# Revit family: 306_ac6e8514f21645dca7f72db6e31d8c
name_source: partatom
category: Pipe Accessories
units: mm (PartAtom-declared; Revit-internal decimal feet)

## family parameters
Always vertical = Yes
Cut with Voids When Loaded = No
Part Type = Valve - Breaks Into
Round Connector Dimension = Use Diameter
Shared = No
Work Plane-Based = No

## types (8) — shared parameters
CAT0 = Yes
CenSd_DN_6 = 6 mm  [stored 0.019685 ft]
DN = 7 mm  [stored 0.0229659 ft]
Description = 3-way rotary mixing valve 3F, PN6 flange
L2D = 265 mm
L2D_Min = 3048 mm
MC = No
Manufacturer = ESBE
QmdConnectorList = 301;D;302;D
R3 = 2 mm  [stored 0.00656168 ft]
URL = http://www.esbe.eu
W2D = 100 mm
X = 3 mm  [stored 0.00984252 ft]
X2 = 5 mm  [stored 0.0164042 ft]
X__ve = -3 mm  [stored -0.00984252 ft]
Y3 = 4 mm  [stored 0.0131234 ft]
magiPartTypeId = 306
magiProductFamilyId = ac6e8514f21645dca7f72db6e31d8c

## per-type parameters (varying)
| type | C | D | D2 | D3 | DN1 | FD2 | H | H1 | LT2 | MH | MH__ve | R1 | R2 | R4 | W1 | X1 | X1__ve | X3 | X5 | Y2 | Y2__ve | Y4 | Z1 | magiProductId |
| 3F 100-225 | 73 mm | 100 mm | 114 mm | 20 mm  [stored 0.0656168 ft] | 16 mm | 105 mm | 132 mm | 106 mm | 133 mm | 90 mm | -90 mm | 60 mm | 57 mm | 75 mm | 16 mm | 18 mm | -18 mm | 213 mm | 80 mm | 38 mm | -38 mm  [stored -0.124672 ft] | 40 mm | 75 mm | 35e6cae2c78145ac8d085347603f0b |
| 3F 125-280 | 80 mm | 125 mm | 138 mm | 23 mm | 18 mm | 120 mm | 150 mm | 121 mm | 150 mm | 108 mm | -108 mm | 72 mm | 69 mm | 90 mm | 11 mm | 21 mm | -21 mm | 243 mm | 91 mm | 38 mm | -38 mm  [stored -0.124672 ft] | 46 mm | 90 mm | 63c3782494ab404eb88c3043804936 |
| 3F 150-400 | 88 mm | 150 mm | 158 mm | 27 mm | 21 mm | 133 mm | 175 mm | 143 mm | 175 mm | 123 mm | -123 mm | 82 mm | 79 mm | 103 mm | 9 mm  [stored 0.0295276 ft] | 24 mm | -24 mm | 286 mm | 107 mm | 37 mm | -37 mm | 54 mm | 103 mm | c360b451805a4af68f699a7088005f |
| 3F 32-28 | 40 mm | 32 mm | 52 mm | 11 mm | 8 mm  [stored 0.0262467 ft] | 60 mm | 80 mm | 57 mm | 80 mm | 44 mm | -44 mm | 29 mm | 26 mm | 37 mm | 14 mm  [stored 0.0459318 ft] | 15 mm  [stored 0.0492126 ft] | -15 mm | 113 mm | 42 mm | 37 mm | -37 mm | 21 mm | 37 mm | fa7e2451a67c46cd9a17dfce243491 |
| 3F 40-44 | 40 mm | 40 mm | 60 mm | 12 mm  [stored 0.0393701 ft] | 9 mm  [stored 0.0295276 ft] | 65 mm | 88 mm | 63 mm | 88 mm | 50 mm | -50 mm | 33 mm | 30 mm | 42 mm | 10 mm  [stored 0.0328084 ft] | 17 mm | -17 mm | 125 mm | 47 mm | 37 mm | -37 mm | 23 mm | 42 mm | 079ccec7fc93466781a61f018673c2 |
| 3F 50-60 | 50 mm | 50 mm | 68 mm | 13 mm | 11 mm | 70 mm | 98 mm | 71 mm | 98 mm | 56 mm | -56 mm | 37 mm | 34 mm | 47 mm | 16 mm | 19 mm | -19 mm | 141 mm | 53 mm | 37 mm | -37 mm | 26 mm | 47 mm | 7cebacd52b384727a93969c1c95a5e |
| 3F 65-90 | 52 mm | 65 mm | 84 mm | 15 mm  [stored 0.0492126 ft] | 12 mm  [stored 0.0393701 ft] | 80 mm | 100 mm | 78 mm | 100 mm | 68 mm | -68 mm  [stored -0.223097 ft] | 45 mm | 42 mm | 57 mm | 10 mm  [stored 0.0328084 ft] | 14 mm  [stored 0.0459318 ft] | -14 mm | 157 mm | 59 mm | 38 mm | -38 mm  [stored -0.124672 ft] | 29 mm | 57 mm | 5ab6774795844029a744bb747653af |
| 3F 80-150 | 63 mm | 80 mm | 98 mm | 18 mm | 14 mm  [stored 0.0459318 ft] | 95 mm | 120 mm | 96 mm | 120 mm | 78 mm | -78 mm  [stored -0.255906 ft] | 52 mm | 49 mm | 65 mm | 14 mm  [stored 0.0459318 ft] | 16 mm | -16 mm | 191 mm | 72 mm | 38 mm | -38 mm  [stored -0.124672 ft] | 36 mm | 65 mm | f56272e02a644ff587acec57c66746 |

note: column(s) folded — value = type name in every type: magiProductCode

note: [stored X ft] marks values corroborated as IEEE doubles in the binary element streams (Revit-internal decimal feet)

## geometry (parser evidence)
native form markers: Sweep x2
no freeform markers — native parametric forms only
